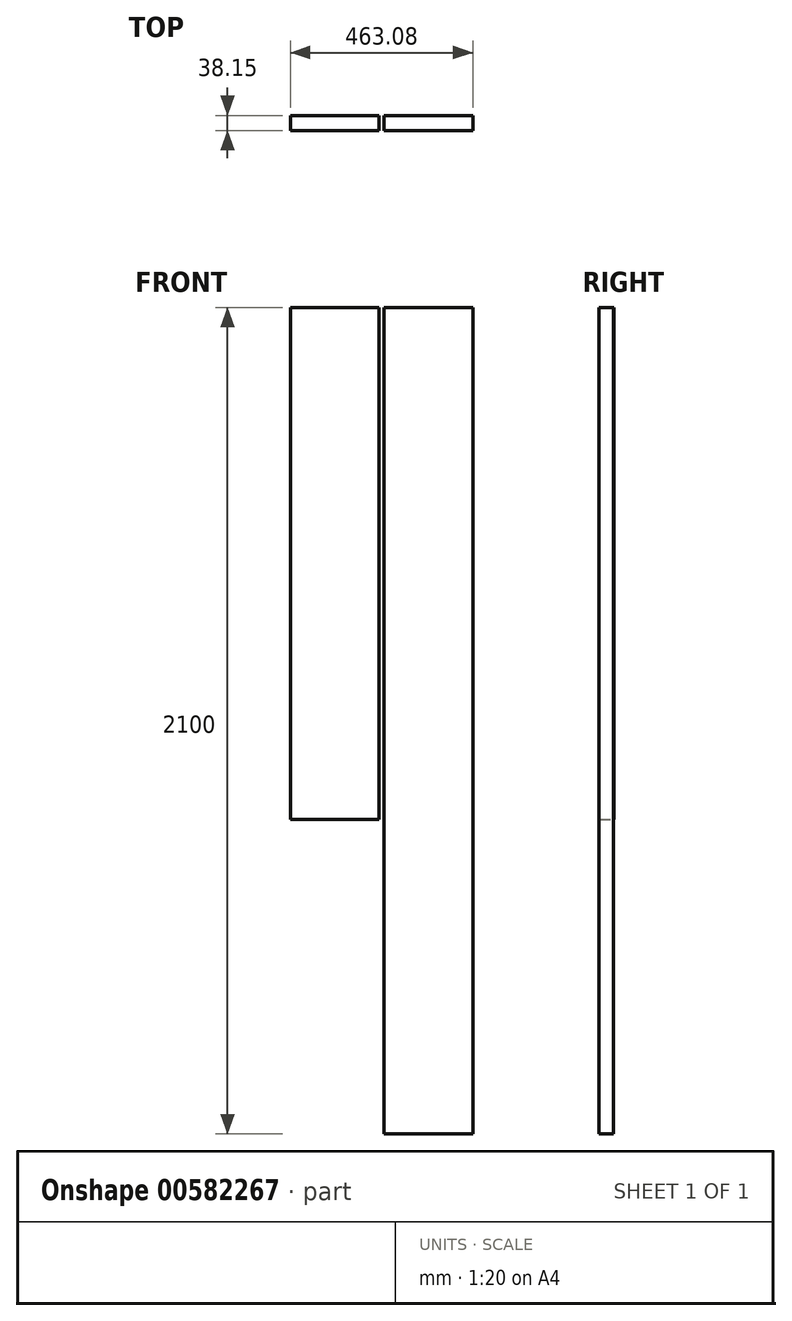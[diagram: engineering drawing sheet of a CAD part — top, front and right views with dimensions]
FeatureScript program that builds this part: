
annotation { "Feature Type Name" : "Feature", "Feature Type Description" : "" }
export const myFeature = defineFeature(function(context is Context, id is Id, definition is map)
    precondition{}
    {
        {
            var Q0;
            Q0=qCreatedBy(makeId("Top.planeOp"),FACE);
            var sketch = newSketch(context, id + "F0", { "sketchPlane" : qUnion([Q0])});
            skLineSegment(sketch, "E0.bottom", {"start": v(-179, -19) * mm, "end": v(46, -19) * mm});
            skLineSegment(sketch, "E0.top", {"start": v(-179, 19) * mm, "end": v(46, 19) * mm});
            skLineSegment(sketch, "E0.left", {"start": v(-179, -19) * mm, "end": v(-179, 19) * mm});
            skLineSegment(sketch, "E0.right", {"start": v(46, -19) * mm, "end": v(46, 19) * mm});
            skPoint(sketch, "E0.middle", {"position": v(-66.5, 0) * mm});
            skLineSegment(sketch, "E1.bottom", {"start": v(-417.08, -18.85) * mm, "end": v(-192.08, -18.85) * mm});
            skLineSegment(sketch, "E1.top", {"start": v(-417.08, 19.15) * mm, "end": v(-192.08, 19.15) * mm});
            skLineSegment(sketch, "E1.left", {"start": v(-417.08, -18.85) * mm, "end": v(-417.08, 19.15) * mm});
            skLineSegment(sketch, "E1.right", {"start": v(-192.08, -18.85) * mm, "end": v(-192.08, 19.15) * mm});
            skPoint(sketch, "E1.middle", {"position": v(-304.58, 0.15) * mm});
            skSolve(sketch);
        }
        {
            var Q0;
            Q0=makeQuery(id+"F0.imprint","IMPRINT",FACE,{"disambiguationData":[TD([[makeQuery(id+"F0.imprint","IMPRINT",EDGE,{"derivedFrom":sQuery(id+"F0.wireOp",EDGE,"E0.bottom")}),1.0]])]});
            extrude(context, id + "F1", {"entities" : qUnion([Q0]), "oppositeDirection" : true, "depth" : 2100 * mm, "offsetDistance" : 25 * mm});
        }
        {
            var Q0;
            Q0=makeQuery(id+"F0.imprint","IMPRINT",FACE,{"disambiguationData":[TD([[makeQuery(id+"F0.imprint","IMPRINT",EDGE,{"derivedFrom":sQuery(id+"F0.wireOp",EDGE,"E1.bottom")}),1.0]])]});
            extrude(context, id + "F2", {"entities" : qUnion([Q0]), "oppositeDirection" : true, "depth" : 1300 * mm, "offsetDistance" : 25 * mm});
        }
    });
